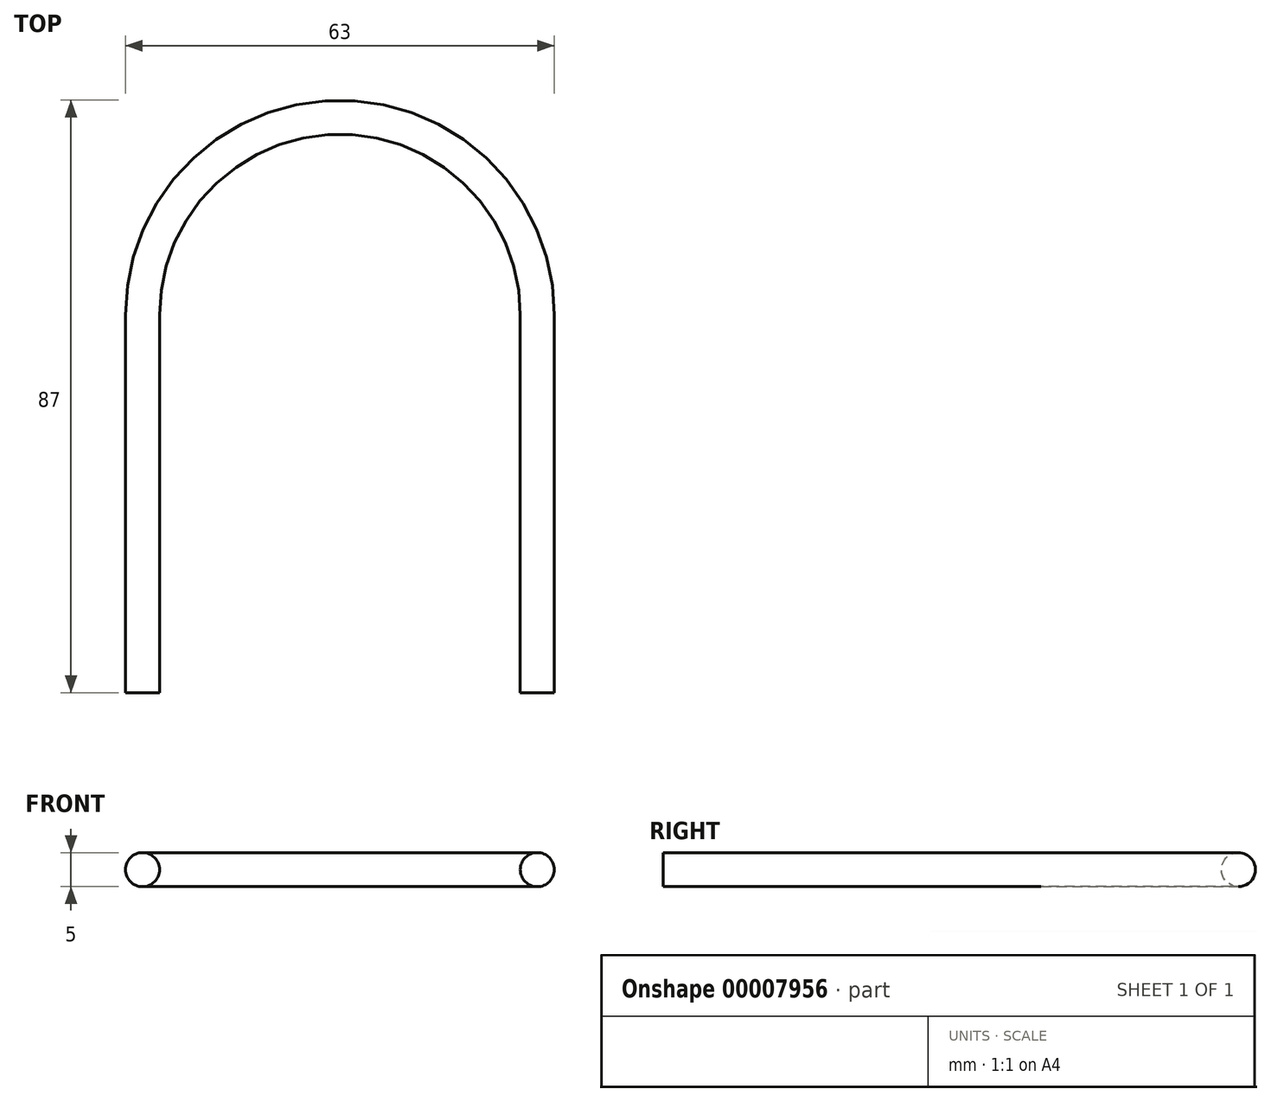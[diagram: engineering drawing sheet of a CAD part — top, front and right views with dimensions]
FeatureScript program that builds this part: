
annotation { "Feature Type Name" : "Feature", "Feature Type Description" : "" }
export const myFeature = defineFeature(function(context is Context, id is Id, definition is map)
    precondition{}
    {
        {
            var Q0;
            Q0=qCreatedBy(makeId("Top.planeOp"),FACE);
            var sketch = newSketch(context, id + "F0", { "sketchPlane" : qUnion([Q0])});
            skLineSegment(sketch, "E0.bottom", {"start": v(0, 0) * mm, "end": v(75, 0) * mm, "construction": true});
            skLineSegment(sketch, "E0.top", {"start": v(0, 85) * mm, "end": v(75, 85) * mm, "construction": true});
            skLineSegment(sketch, "E0.left", {"start": v(0, 0) * mm, "end": v(0, 85) * mm, "construction": true});
            skLineSegment(sketch, "E0.right", {"start": v(75, 0) * mm, "end": v(75, 85) * mm, "construction": true});
            skLineSegment(sketch, "E1", {"start": v(37.5, 85) * mm, "end": v(37.5, 0) * mm, "construction": true});
            skCircle(sketch, "E2", {"center": v(37.5, 47.5) * mm, "radius": 31.5 * mm, "construction": true});
            skLineSegment(sketch, "E3", {"start": v(37.5, 79) * mm, "end": v(37.5, 85) * mm, "construction": true});
            skLineSegment(sketch, "E4", {"start": v(6, 47.5) * mm, "end": v(0, 47.5) * mm, "construction": true});
            skArc(sketch, "E5", {"start": v(69, 47.5) * mm, "mid": v(37.5, 79) * mm, "end": v(6, 47.5) * mm});
            skLineSegment(sketch, "E6", {"start": v(6, 47.5) * mm, "end": v(6, -8) * mm});
            skLineSegment(sketch, "E7", {"start": v(6, -8) * mm, "end": v(11, -8) * mm});
            skLineSegment(sketch, "E8", {"start": v(11, -8) * mm, "end": v(11, 47.5) * mm});
            skLineSegment(sketch, "E9.0.MirrorCS", {"start": v(69, 47.5) * mm, "end": v(69, -8) * mm});
            skLineSegment(sketch, "E9.1.MirrorCS", {"start": v(64, -8) * mm, "end": v(64, 47.5) * mm});
            skLineSegment(sketch, "E9.2.MirrorCS", {"start": v(69, -8) * mm, "end": v(64, -8) * mm});
            skArc(sketch, "E10", {"start": v(64, 47.5) * mm, "mid": v(37.5, 74) * mm, "end": v(11, 47.5) * mm});
            skSolve(sketch);
        }
        {
            var Q0;
            Q0 = qSketchRegion(id + "F0", true);
            extrude(context, id + "F1", {"entities" : qUnion([Q0]), "depth" : 5 * mm});
        }
        {
            var Q0;
            Q0=makeQuery(id+"F1.opExtrude","CAP_EDGE",EDGE,{"disambiguationData":[OSD([sQuery(id+"F0.wireOp",EDGE,"E5")])],"isStart":false});
            var Q1;
            Q1=makeQuery(id+"F1.opExtrude","CAP_EDGE",EDGE,{"disambiguationData":[OSD([sQuery(id+"F0.wireOp",EDGE,"E10")])],"isStart":false});
            var Q2;
            Q2=makeQuery(id+"F1.opExtrude","CAP_EDGE",EDGE,{"disambiguationData":[OSD([sQuery(id+"F0.wireOp",EDGE,"E6")])],"isStart":true});
            var Q3;
            Q3=makeQuery(id+"F1.opExtrude","CAP_EDGE",EDGE,{"disambiguationData":[OSD([sQuery(id+"F0.wireOp",EDGE,"E8")])],"isStart":true});
            fillet(context, id + "F2", {"entities" : qUnion([Q0, Q1, Q2, Q3]), "radius" : 2.5 * mm, "tangentPropagation" : true, "allowEdgeOverflow" : false});
        }
    });
